# Revit family: FLOWAIR Elis G1-2RW-200_RFA_2019
name_source: partatom
category: Mechanical Equipment
units: mm (PartAtom-declared; Revit-internal decimal feet)

## family parameters
Always vertical = No
Cut with Voids When Loaded = No
Part Type = Normal
Room Calculation Point = No
Round Connector Dimension = Use Diameter
Shared = No
Work Plane-Based = No

## types (1)
- Elis G1-2RW-200
    Air flow = 0.0 L/s
    Apparent load = 0 VA
    Connection = 3/4"
    Description = Vratová clona
    Heating capacity = 0 W
    IP = 54
    Inlet air temperature = 0 °C
    Inlet water temperature = 0 °C
    Load classification = Motor
    Manufacturer = Hydronic Systems Prague s.r.o.
    Material = FLOWAIR-Galvanized steel
    Max current consumption = 0 A
    Model = Elis G1-2RW-200
    Outlet air temperature = 0 °C
    Outlet water temperature = 0 °C
    Power ratio = 0.98
    Power supply = 230 V
    Product data = 14293; délka 200cm, 2 řadý výměník - vodní ohřev (130°C; PN16)
    Type Comments = vnitřní instalace mimo prostor s nebezpečím výbuchu, IP54; max dosah 7,5m na 3 rychlost
    URL = www.hydronic.cz
    Water pressure drop in the heat exchanger = 0.0 Pa
    Water stream flow in the heat exchanger = 0.0 L/s
    Weight of unit = 62.00 kg
    Weight of unit filled with water = 64.30 kg

## geometry (parser evidence)
native form markers: Sweep x3
no freeform markers — native parametric forms only
